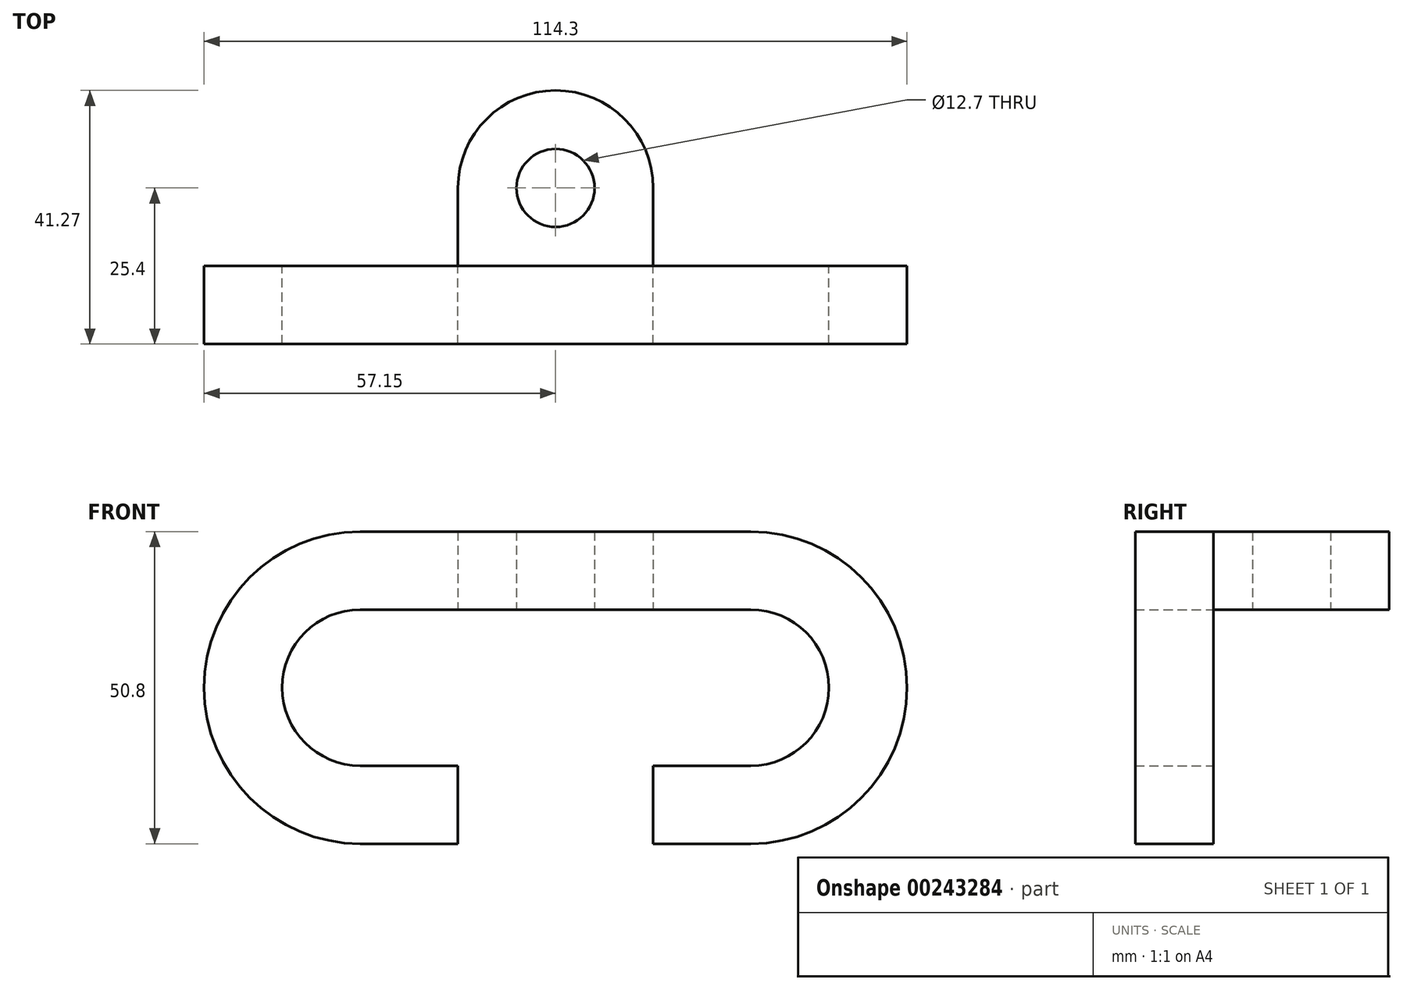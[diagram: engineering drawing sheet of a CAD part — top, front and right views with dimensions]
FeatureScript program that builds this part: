
annotation { "Feature Type Name" : "Feature", "Feature Type Description" : "" }
export const myFeature = defineFeature(function(context is Context, id is Id, definition is map)
    precondition{}
    {
        {
            var Q0;
            Q0=qCreatedBy(makeId("Front.planeOp"),FACE);
            var sketch = newSketch(context, id + "F0", { "sketchPlane" : qUnion([Q0])});
            skArc(sketch, "E0", {"start": v(31.75, -25.4) * mm, "mid": v(57.15, 0) * mm, "end": v(31.75, 25.4) * mm});
            skLineSegment(sketch, "E1", {"start": v(31.75, 25.4) * mm, "end": v(0, 25.4) * mm});
            skLineSegment(sketch, "E2", {"start": v(31.75, -25.4) * mm, "end": v(15.88, -25.4) * mm});
            skLineSegment(sketch, "E3", {"start": v(31.75, 12.7) * mm, "end": v(0, 12.7) * mm});
            skLineSegment(sketch, "E4", {"start": v(31.75, -12.7) * mm, "end": v(15.88, -12.7) * mm});
            skArc(sketch, "E5", {"start": v(31.75, -12.7) * mm, "mid": v(44.45, 0) * mm, "end": v(31.75, 12.7) * mm});
            skLineSegment(sketch, "E6", {"start": v(15.88, -12.7) * mm, "end": v(15.88, -25.4) * mm});
            skPoint(sketch, "E7.orphan", {"position": v(0, -12.7) * mm});
            skPoint(sketch, "E8.orphan", {"position": v(0, -25.4) * mm});
            skLineSegment(sketch, "E9.MirrorCS", {"start": v(-31.75, 25.4) * mm, "end": v(0, 25.4) * mm});
            skLineSegment(sketch, "E10.MirrorCS", {"start": v(-31.75, 12.7) * mm, "end": v(0, 12.7) * mm});
            skArc(sketch, "E11.MirrorCS", {"start": v(-31.75, -12.7) * mm, "mid": v(-44.45, 0) * mm, "end": v(-31.75, 12.7) * mm});
            skArc(sketch, "E12.MirrorCS", {"start": v(-31.75, -25.4) * mm, "mid": v(-57.15, 0) * mm, "end": v(-31.75, 25.4) * mm});
            skLineSegment(sketch, "E13.MirrorCS", {"start": v(-31.75, -12.7) * mm, "end": v(-15.88, -12.7) * mm});
            skLineSegment(sketch, "E14.MirrorCS", {"start": v(-31.75, -25.4) * mm, "end": v(-15.88, -25.4) * mm});
            skLineSegment(sketch, "E15.MirrorCS", {"start": v(-15.88, -12.7) * mm, "end": v(-15.88, -25.4) * mm});
            skSolve(sketch);
        }
        {
            var Q0;
            Q0 = qSketchRegion(id + "F0", true);
            extrude(context, id + "F1", {"entities" : qUnion([Q0]), "depth" : 12.7 * mm});
        }
        {
            var Q0;
            Q0=makeQuery(id+"F1.opExtrude","SWEPT_FACE",FACE,{"disambiguationData":[OSD([sQuery(id+"F0.wireOp",EDGE,"E3"),sQuery(id+"F0.wireOp",EDGE,"E10.MirrorCS")])]});
            var sketch = newSketch(context, id + "F2", { "sketchPlane" : qUnion([Q0])});
            skCircle(sketch, "E16", {"center": v(0, -12.7) * mm, "radius": 6.35 * mm});
            skArc(sketch, "E17", {"start": v(-15.88, -12.7) * mm, "mid": v(0, -28.57) * mm, "end": v(15.88, -12.7) * mm});
            skLineSegment(sketch, "E18", {"start": v(-15.88, -12.7) * mm, "end": v(-15.88, 0) * mm});
            skLineSegment(sketch, "E19", {"start": v(15.88, -12.7) * mm, "end": v(15.88, 0) * mm});
            skLineSegment(sketch, "E20", {"start": v(-15.88, 0) * mm, "end": v(15.88, 0) * mm});
            skSolve(sketch);
        }
        {
            var Q0;
            Q0=makeQuery(id+"F2.imprint","IMPRINT",FACE,{"disambiguationData":[TD([[makeQuery(id+"F2.imprint","IMPRINT",EDGE,{"derivedFrom":sQuery(id+"F2.wireOp",EDGE,"E16")}),-1.0]])]});
            extrude(context, id + "F3", {"entities" : qUnion([Q0]), "oppositeDirection" : true, "depth" : 12.7 * mm});
        }
    });
